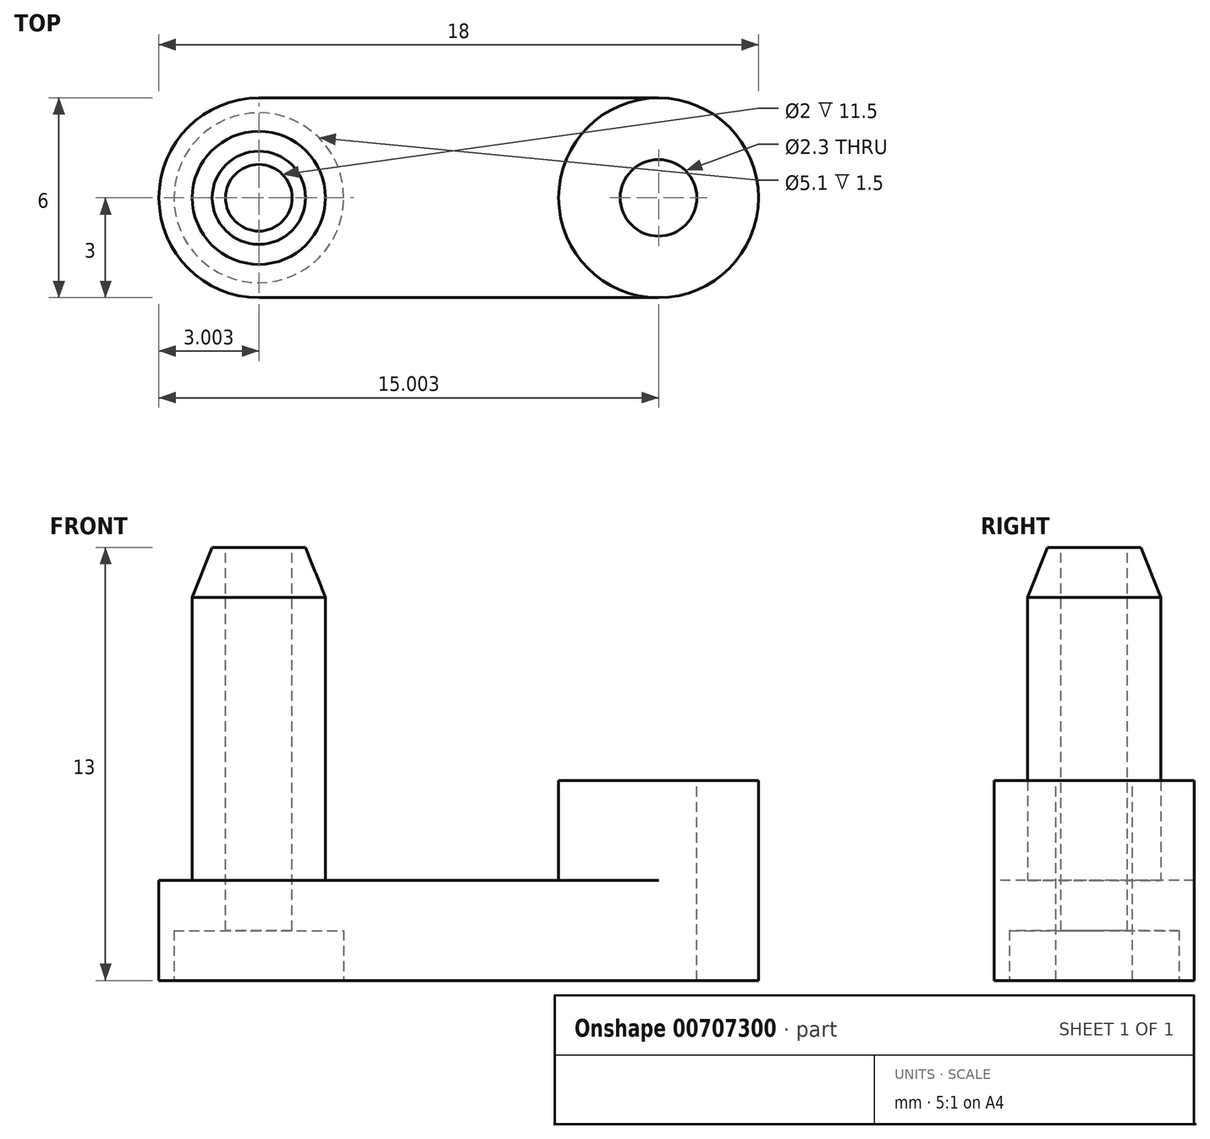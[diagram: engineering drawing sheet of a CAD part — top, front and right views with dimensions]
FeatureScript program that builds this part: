
annotation { "Feature Type Name" : "Feature", "Feature Type Description" : "" }
export const myFeature = defineFeature(function(context is Context, id is Id, definition is map)
    precondition{}
    {
        {
            var Q0;
            Q0=qCreatedBy(makeId("Top.planeOp"),FACE);
            var sketch = newSketch(context, id + "F0", { "sketchPlane" : qUnion([Q0])});
            skLineSegment(sketch, "E0.bottom", {"start": v(-7.1, 3) * mm, "end": v(10.9, 3) * mm});
            skLineSegment(sketch, "E0.top", {"start": v(-7.1, -3) * mm, "end": v(10.9, -3) * mm});
            skLineSegment(sketch, "E0.left", {"start": v(-7.1, 3) * mm, "end": v(-7.1, -3) * mm});
            skLineSegment(sketch, "E0.right", {"start": v(10.9, 3) * mm, "end": v(10.9, -3) * mm});
            skSolve(sketch);
        }
        {
            var Q0;
            Q0=qSketchRegion(id+"F0",true);
            extrude(context, id + "F1", {"entities" : qUnion([Q0]), "depth" : 3 * mm, "offsetDistance" : 25 * mm});
        }
        {
            var Q0;
            Q0=makeQuery(id+"F1.opExtrude","CAP_FACE",FACE,{"disambiguationData":[OSD([sQuery(id+"F0.wireOp",EDGE,"E0.bottom"),sQuery(id+"F0.wireOp",EDGE,"E0.top"),sQuery(id+"F0.wireOp",EDGE,"E0.left"),sQuery(id+"F0.wireOp",EDGE,"E0.right")])],"isStart":false});
            var sketch = newSketch(context, id + "F2", { "sketchPlane" : qUnion([Q0])});
            skCircle(sketch, "E1", {"center": v(7.9, 0) * mm, "radius": 3 * mm});
            skCircle(sketch, "E2", {"center": v(-4.1, 0) * mm, "radius": 2 * mm});
            skSolve(sketch);
        }
        {
            var Q0;
            Q0=qSketchRegion(id+"F2",true);
            extrude(context, id + "F3", {"entities" : qUnion([Q0]), "operationType" : NewBodyOperationType.ADD, "depth" : 10 * mm, "offsetDistance" : 25 * mm});
        }
        {
            var Q0;
            Q0=makeQuery(id+"F3.opExtrude","CAP_FACE",FACE,{"disambiguationData":[OSD([sQuery(id+"F2.wireOp",EDGE,"E2")])],"isStart":false});
            var sketch = newSketch(context, id + "F4", { "sketchPlane" : qUnion([Q0])});
            skCircle(sketch, "E3", {"center": v(-4.1, 0) * mm, "radius": 1 * mm});
            skCircle(sketch, "E4", {"center": v(7.9, 0) * mm, "radius": 1.15 * mm});
            skSolve(sketch);
        }
        {
            var Q0;
            Q0=qSketchRegion(id+"F4",true);
            extrude(context, id + "F5", {"entities" : qUnion([Q0]), "operationType" : NewBodyOperationType.REMOVE, "oppositeDirection" : true, "depth" : 20 * mm, "offsetDistance" : 25 * mm});
        }
        {
            var Q0;
            Q0=makeQuery(id+"F3.opExtrude","CAP_EDGE",EDGE,{"disambiguationData":[OSD([sQuery(id+"F2.wireOp",EDGE,"E2")])],"isStart":false});
            chamfer(context, id + "F6", {"entities" : qUnion([Q0]), "chamferType" : ChamferType.TWO_OFFSETS, "width1" : 0.6 * mm, "oppositeDirection" : false, "width2" : 1.5 * mm, "tangentPropagation" : true});
        }
        {
            var Q0;
            Q0=makeQuery(id+"F3.opExtrude","CAP_FACE",FACE,{"disambiguationData":[OSD([sQuery(id+"F2.wireOp",EDGE,"E1")])],"isStart":false});
            var sketch = newSketch(context, id + "F7", { "sketchPlane" : qUnion([Q0])});
            skLineSegment(sketch, "E5.bottom", {"start": v(1.79, 5.38) * mm, "end": v(13.39, 5.38) * mm});
            skLineSegment(sketch, "E5.top", {"start": v(1.79, -6.45) * mm, "end": v(13.39, -6.45) * mm});
            skLineSegment(sketch, "E5.left", {"start": v(1.79, 5.38) * mm, "end": v(1.79, -6.45) * mm});
            skLineSegment(sketch, "E5.right", {"start": v(13.39, 5.38) * mm, "end": v(13.39, -6.45) * mm});
            skSolve(sketch);
        }
        {
            var Q0;
            Q0=qSketchRegion(id+"F7",true);
            extrude(context, id + "F8", {"entities" : qUnion([Q0]), "operationType" : NewBodyOperationType.REMOVE, "oppositeDirection" : true, "depth" : 7 * mm, "offsetDistance" : 25 * mm});
        }
        {
            var Q0;
            Q0=makeQuery(id+"F1.opExtrude","SWEPT_EDGE",EDGE,{"disambiguationData":[OSD([sQuery(id+"F0.wireOp",EDGE,"E0.top"),sQuery(id+"F0.wireOp",EDGE,"E0.right")])]});
            var Q1;
            Q1=makeQuery(id+"F1.opExtrude","SWEPT_EDGE",EDGE,{"disambiguationData":[OSD([sQuery(id+"F0.wireOp",EDGE,"E0.bottom"),sQuery(id+"F0.wireOp",EDGE,"E0.right")])]});
            var Q2;
            Q2=makeQuery(id+"F1.opExtrude","SWEPT_EDGE",EDGE,{"disambiguationData":[OSD([sQuery(id+"F0.wireOp",EDGE,"E0.bottom"),sQuery(id+"F0.wireOp",EDGE,"E0.left")])]});
            var Q3;
            Q3=makeQuery(id+"F1.opExtrude","SWEPT_EDGE",EDGE,{"disambiguationData":[OSD([sQuery(id+"F0.wireOp",EDGE,"E0.top"),sQuery(id+"F0.wireOp",EDGE,"E0.left")])]});
            fillet(context, id + "F9", {"entities" : qUnion([Q0, Q1, Q2, Q3]), "radius" : 3 * mm, "tangentPropagation" : true, "allowEdgeOverflow" : false});
        }
        {
            var Q0;
            Q0=makeQuery(id+"F1.opExtrude","CAP_FACE",FACE,{"disambiguationData":[OSD([sQuery(id+"F0.wireOp",EDGE,"E0.bottom"),sQuery(id+"F0.wireOp",EDGE,"E0.top"),sQuery(id+"F0.wireOp",EDGE,"E0.left"),sQuery(id+"F0.wireOp",EDGE,"E0.right")])],"isStart":true});
            var sketch = newSketch(context, id + "F10", { "sketchPlane" : qUnion([Q0])});
            skCircle(sketch, "E6", {"center": v(-4.1, 0) * mm, "radius": 2.55 * mm});
            skCircle(sketch, "E7", {"center": v(-4.1, 0) * mm, "radius": 1 * mm});
            skSolve(sketch);
        }
        {
            var Q0;
            Q0=qSketchRegion(id+"F10",true);
            extrude(context, id + "F11", {"entities" : qUnion([Q0]), "operationType" : NewBodyOperationType.REMOVE, "oppositeDirection" : true, "depth" : 1.5 * mm, "offsetDistance" : 25 * mm});
        }
    });
